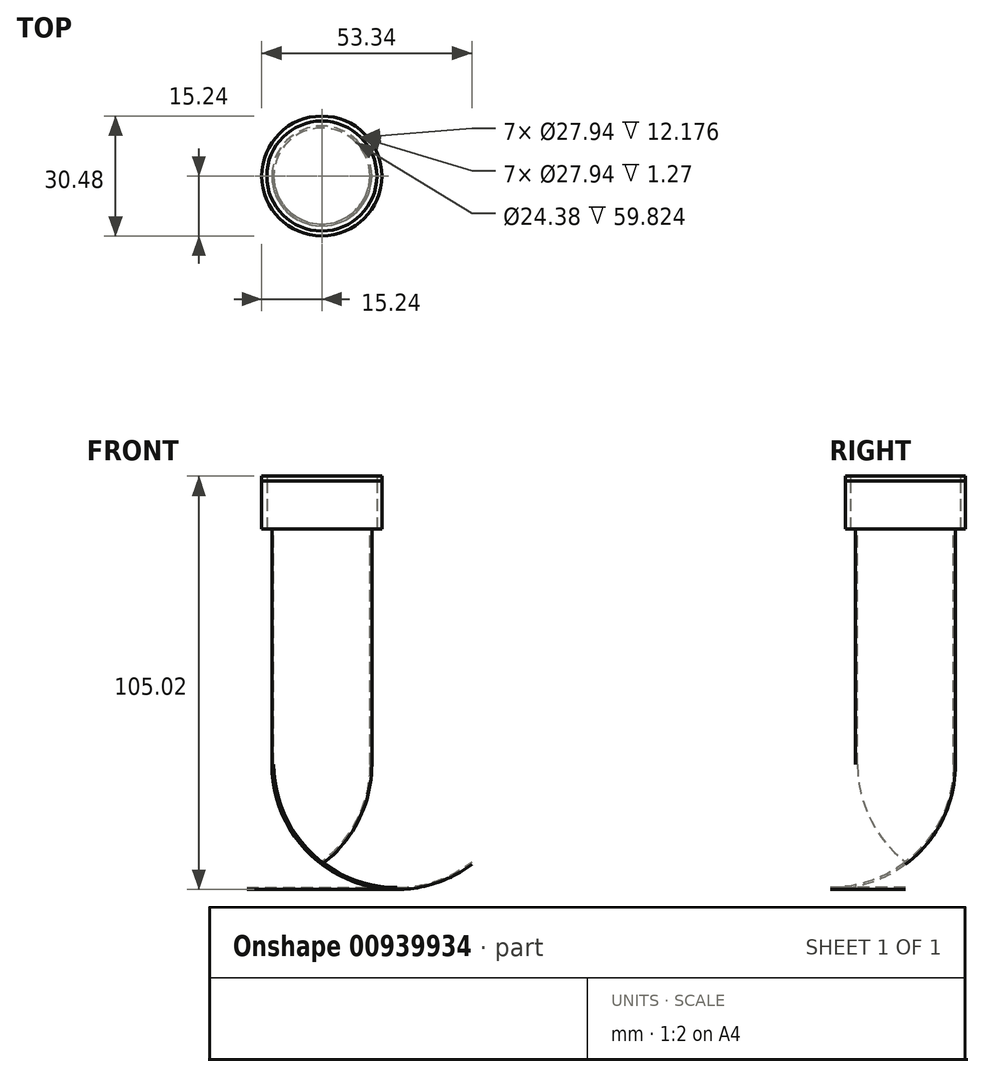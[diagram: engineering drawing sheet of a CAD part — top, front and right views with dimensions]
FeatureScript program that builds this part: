
annotation { "Feature Type Name" : "Feature", "Feature Type Description" : "" }
export const myFeature = defineFeature(function(context is Context, id is Id, definition is map)
    precondition{}
    {
        {
            var Q0;
            Q0=qCreatedBy(makeId("Front.planeOp"),FACE);
            var sketch = newSketch(context, id + "F0", { "sketchPlane" : qUnion([Q0])});
            skLineSegment(sketch, "E0.bottom", {"start": v(0, 39.83) * mm, "end": v(-25.4, 39.83) * mm});
            skLineSegment(sketch, "E0.top", {"start": v(0, -20) * mm, "end": v(-25.4, -20) * mm});
            skLineSegment(sketch, "E0.left", {"start": v(0, 39.83) * mm, "end": v(0, -20) * mm});
            skLineSegment(sketch, "E0.right", {"start": v(-25.4, 39.83) * mm, "end": v(-25.4, -20) * mm});
            skLineSegment(sketch, "E1.bottom", {"start": v(-25.4, -20) * mm, "end": v(0, -20) * mm});
            skPoint(sketch, "E2.oppositeSnap0", {"position": v(-12.7, 39.83) * mm});
            skLineSegment(sketch, "E2.bottom", {"start": v(-27.94, 53.28) * mm, "end": v(2.54, 53.28) * mm});
            skLineSegment(sketch, "E2.top", {"start": v(-27.94, 39.83) * mm, "end": v(2.54, 39.83) * mm});
            skLineSegment(sketch, "E2.left", {"start": v(-27.94, 53.28) * mm, "end": v(-27.94, 39.83) * mm});
            skLineSegment(sketch, "E2.right", {"start": v(2.54, 53.28) * mm, "end": v(2.54, 39.83) * mm});
            skLineSegment(sketch, "E3", {"start": v(-12.7, 39.83) * mm, "end": v(-12.7, -20) * mm});
            skLineSegment(sketch, "E4", {"start": v(-12.7, 39.83) * mm, "end": v(-12.7, 53.28) * mm});
            skPoint(sketch, "E5.end.orphan", {"position": v(-12.7, -45.4) * mm});
            skLineSegment(sketch, "E6", {"start": v(-12.7, -20) * mm, "end": v(-12.7, -45.4) * mm});
            skArc(sketch, "E7", {"start": v(-12.7, -45.4) * mm, "mid": v(-3.35, -34.2) * mm, "end": v(0, -20) * mm});
            skPoint(sketch, "E8.orphan", {"position": v(-25.4, -45.4) * mm});
            skPoint(sketch, "E1.top.end.orphan", {"position": v(0, -45.4) * mm});
            skLineSegment(sketch, "E9.0", {"start": v(-0.5, 39.83) * mm, "end": v(-0.5, -20) * mm});
            skArc(sketch, "E10.0", {"start": v(-13, -44.99) * mm, "mid": v(-3.8, -33.97) * mm, "end": v(-0.5, -20) * mm});
            skLineSegment(sketch, "E11.0", {"start": v(1.27, 53.28) * mm, "end": v(1.27, 39.83) * mm});
            skLineSegment(sketch, "E12.0", {"start": v(-27.94, 52) * mm, "end": v(2.54, 52) * mm});
            skSolve(sketch);
        }
        {
            var Q0;
            {var subQ0=sQuery(id+"F0.wireOp",EDGE,"E2.right");var subQ1=sQuery(id+"F0.wireOp",EDGE,"E2.top");var subQ2=makeQuery(id+"F0.imprint","INTERSECT",VERTEX,{"derivedFrom":[subQ1,subQ0]});Q0=makeQuery(id+"F0.imprint","IMPRINT",FACE,{"disambiguationData":[TD([[makeQuery(id+"F0.imprint","IMPRINT",EDGE,{"disambiguationData":[TD([[subQ2,1.0]])],"derivedFrom":subQ1}),1.0]])]});}
            var Q1;
            Q1=sQuery(id+"F0.wireOp",EDGE,"E4");
            revolve(context, id + "F1", {"surfaceOperationType" : NewSurfaceOperationType.NEW, "entities" : qUnion([Q0]), "axis" : qUnion([Q1]), "revolveType" : RevolveType.FULL});
        }
        {
            var Q0;
            {var subQ0=sQuery(id+"F0.wireOp",EDGE,"E0.left");Q0=makeQuery(id+"F0.imprint","IMPRINT",FACE,{"disambiguationData":[TD([[makeQuery(id+"F0.imprint","IMPRINT",EDGE,{"derivedFrom":subQ0}),-1.0]])]});}
            var Q1;
            Q1=sQuery(id+"F0.wireOp",EDGE,"E3");
            revolve(context, id + "F2", {"surfaceOperationType" : NewSurfaceOperationType.NEW, "entities" : qUnion([Q0]), "axis" : qUnion([Q1]), "revolveType" : RevolveType.FULL});
        }
        {
            var Q0;
            {var subQ0=sQuery(id+"F0.wireOp",EDGE,"E4");var subQ1=sQuery(id+"F0.wireOp",EDGE,"E2.bottom");var subQ2=makeQuery(id+"F0.imprint","INTERSECT",VERTEX,{"derivedFrom":[subQ1,subQ0]});Q0=makeQuery(id+"F0.imprint","IMPRINT",FACE,{"disambiguationData":[TD([[makeQuery(id+"F0.imprint","IMPRINT",EDGE,{"disambiguationData":[TD([[subQ2,-1.0]])],"derivedFrom":subQ1}),-1.0]])]});}
            var Q1;
            Q1=sQuery(id+"F0.wireOp",EDGE,"E4");
            revolve(context, id + "F3", {"surfaceOperationType" : NewSurfaceOperationType.NEW, "entities" : qUnion([Q0]), "axis" : qUnion([Q1]), "revolveType" : RevolveType.FULL});
        }
        {
            var Q0;
            {var subQ0=sQuery(id+"F0.wireOp",EDGE,"E2.right");var subQ1=sQuery(id+"F0.wireOp",EDGE,"E2.bottom");var subQ2=makeQuery(id+"F0.imprint","INTERSECT",VERTEX,{"derivedFrom":[subQ1,subQ0]});Q0=makeQuery(id+"F0.imprint","IMPRINT",FACE,{"disambiguationData":[TD([[makeQuery(id+"F0.imprint","IMPRINT",EDGE,{"disambiguationData":[TD([[subQ2,1.0]])],"derivedFrom":subQ1}),-1.0]])]});}
            var Q1;
            Q1=sQuery(id+"F0.wireOp",EDGE,"E4");
            revolve(context, id + "F4", {"surfaceOperationType" : NewSurfaceOperationType.NEW, "entities" : qUnion([Q0]), "axis" : qUnion([Q1]), "revolveType" : RevolveType.FULL});
        }
        {
            var Q0;
            {var subQ0=sQuery(id+"F0.wireOp",EDGE,"E7");Q0=makeQuery(id+"F0.imprint","IMPRINT",FACE,{"disambiguationData":[TD([[makeQuery(id+"F0.imprint","IMPRINT",EDGE,{"derivedFrom":subQ0}),1.0]])]});}
            var Q1;
            Q1=sQuery(id+"F0.wireOp",EDGE,"E6");
            revolve(context, id + "F5", {"operationType" : NewBodyOperationType.ADD, "surfaceOperationType" : NewSurfaceOperationType.NEW, "entities" : qUnion([Q0]), "axis" : qUnion([Q1]), "revolveType" : RevolveType.FULL});
        }
    });
